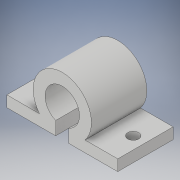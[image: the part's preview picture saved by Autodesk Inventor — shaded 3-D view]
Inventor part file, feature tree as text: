
AUTODESK INVENTOR PART (.ipt)
format: ipt  version: 2019 (Build 230136000, 136)  size: 124,928 bytes
history: native  units: mm
features: extrude x2, sketch x2, other x1
ambient origin geometry x8: Origin, YZ Plane, XZ Plane, XY Plane, X Axis, Y Axis, Z Axis, Center Point
bodies: Body1 (feature_tree)
feature tree (5):
  other  "ソリッド1"
  extrude  "押し出し1"  Depth=6.2mm
  extrude  "押し出し2"  Depth=10.5mm
  sketch  "スケッチ1"
  sketch  "スケッチ2"
